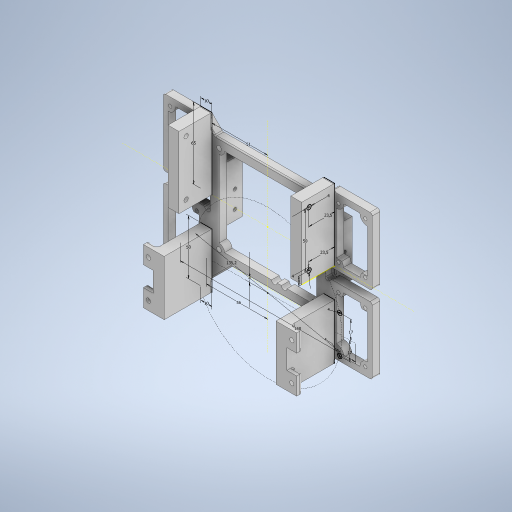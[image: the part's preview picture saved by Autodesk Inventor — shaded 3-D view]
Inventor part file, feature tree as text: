
AUTODESK INVENTOR PART (.ipt)
format: ipt  version: 2024.2 (Build 282272000, 272)  size: 873,984 bytes
history: native  units: mm
features: extrude x7, fillet x6, sketch x6, other x1
ambient origin geometry x8: Origin, YZ Plane, XZ Plane, XY Plane, X Axis, Y Axis, Z Axis, Center Point
bodies: Body1 (feature_tree)
feature tree (20):
  other  "Bryła1"
  extrude  "Wyciągnięcie proste1"  Depth=105.0mm
  fillet  "Zaokrąglenie1"  Radius=96.0mm
  extrude  "Wyciągnięcie proste2"  Depth=7.0mm TaperAngle=0.0deg
  fillet  "Zaokrąglenie2"  Radius=89.0mm
  extrude  "Wyciągnięcie proste3"  Depth=80.0mm
  sketch  "Szkic4"
  extrude  "Wyciągnięcie proste4"  Depth=2.5mm
  fillet  "Zaokrąglenie3"  Radius=15.0mm
  fillet  "Zaokrąglenie4"  Radius=2.5mm
  extrude  "Wyciągnięcie proste5"  Depth=9.0mm
  extrude  "Wyciągnięcie proste6"  Depth=5.0mm
  fillet  "Zaokrąglenie5"  Radius=5.0mm
  extrude  "Wyciągnięcie proste7"  Depth=5.0mm
  fillet  "Zaokrąglenie6"  Radius=5.0mm
  sketch  "Szkic1"
  sketch  "Szkic2"
  sketch  "Szkic3"
  sketch  "Szkic5"
  sketch  "Szkic6"
